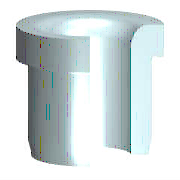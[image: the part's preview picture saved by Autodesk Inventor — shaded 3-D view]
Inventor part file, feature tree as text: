
AUTODESK INVENTOR PART (.ipt)
format: ipt  version: 2023.3 (Build 273359000, 359)  size: 182,784 bytes
history: native  units: mm (DEFAULTED — no unit token found)
features: other x1, plane x1, hole x1, sketch x1
ambient origin geometry x8: Origin, YZ Plane, XZ Plane, XY Plane, X Axis, Y Axis, Z Axis, Center Point
bodies: Solid1 (feature_tree)
feature tree (4):
  other  "Körper"
  plane  "Arbeitsebene1"
  hole  "Bohrung1"  [1 undecoded]
  sketch  "Skizze2"  dims[d0=9.0mm d1=6.0mm d2=12.0mm d3=2.094395mm d4=0.4mm d5=0.1mm d6=2.0mm d7=15.0deg d8=0.2mm d9=0.4mm d10=2.5mm d11=3.0mm d22=90.0deg d12=1.0mm d13=15.0deg d14=1.0mm d15=0.0mm d16=0.0mm d17=0.0mm d29=1.0mm d30=3.0mm d32=0.5mm d33=6.0mm d34=1.0mm d35=2.0mm d36=3.490659mm d37=8.0mm d38=20.594885mm d39=6.0mm]
note: 1 required parameter value undecoded (feature->parameter linkage not recoverable at this tier; creation-order binding heuristic only, values carry confidence <= 0.55)
